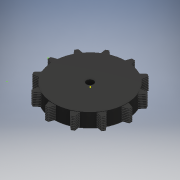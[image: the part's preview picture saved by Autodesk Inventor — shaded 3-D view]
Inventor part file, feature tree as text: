
AUTODESK INVENTOR PART (.ipt)
format: ipt  version: 2018 (Build 220112000, 112)  size: 537,088 bytes
history: native  units: mm
features: sketch x17, extrude x6, pattern_linear x1, pattern_circular x1
ambient origin geometry x8: Origin, YZ Plane, XZ Plane, XY Plane, X Axis, Y Axis, Z Axis, Center Point
bodies: Solid1 (feature_tree)
feature tree (25):
  sketch  "Sketch1"  dims[d0=1000.0mm d1=200.0mm d2=0.0mm]
  sketch  "Sketch2"  dims[d18=10.0mm d19=0.0mm d20=20.0mm d21=0.0mm]
  extrude  "Extrusion1"  Depth=1000.0mm TaperAngle=0.0deg
  extrude  "Extrusion2"  Depth=20.0mm TaperAngle=0.0deg
  sketch  "Sketch4"  dims[d31=200.0mm d32=0.0mm d33=2000.0mm d34=0.0mm]
  sketch  "Sketch5"
  extrude  "Extrusion3"  Depth=120.0mm TaperAngle=360.0deg
  pattern_linear  "Rectangular Pattern1"  Count1=100 Spacing1=0.0mm
  sketch  "Sketch7"
  sketch  "Sketch8"
  sketch  "Sketch9"
  sketch  "Sketch10"
  sketch  "Sketch11"
  pattern_circular  "Circular Pattern1"  Count=10  [1 undecoded]
  extrude  "Extrusion4"  Depth=2000.0mm TaperAngle=0.0deg
  extrude  "Extrusion5"  [1 undecoded]
  sketch  "Sketch14"
  sketch  "Sketch15"
  extrude  "Extrusion6"  [1 undecoded]
  sketch  "Sketch17"
  sketch  "Sketch3"  dims[d22=100.0mm d24=20.0mm d25=120.0mm d26=360.0deg d28=1000.0mm d29=0.0mm d30=100.0mm]
  sketch  "Sketch6"
  sketch  "Sketch12"
  sketch  "Sketch13"
  sketch  "Sketch16"
note: 3 required parameter values undecoded (feature->parameter linkage not recoverable at this tier; creation-order binding heuristic only, values carry confidence <= 0.55)
